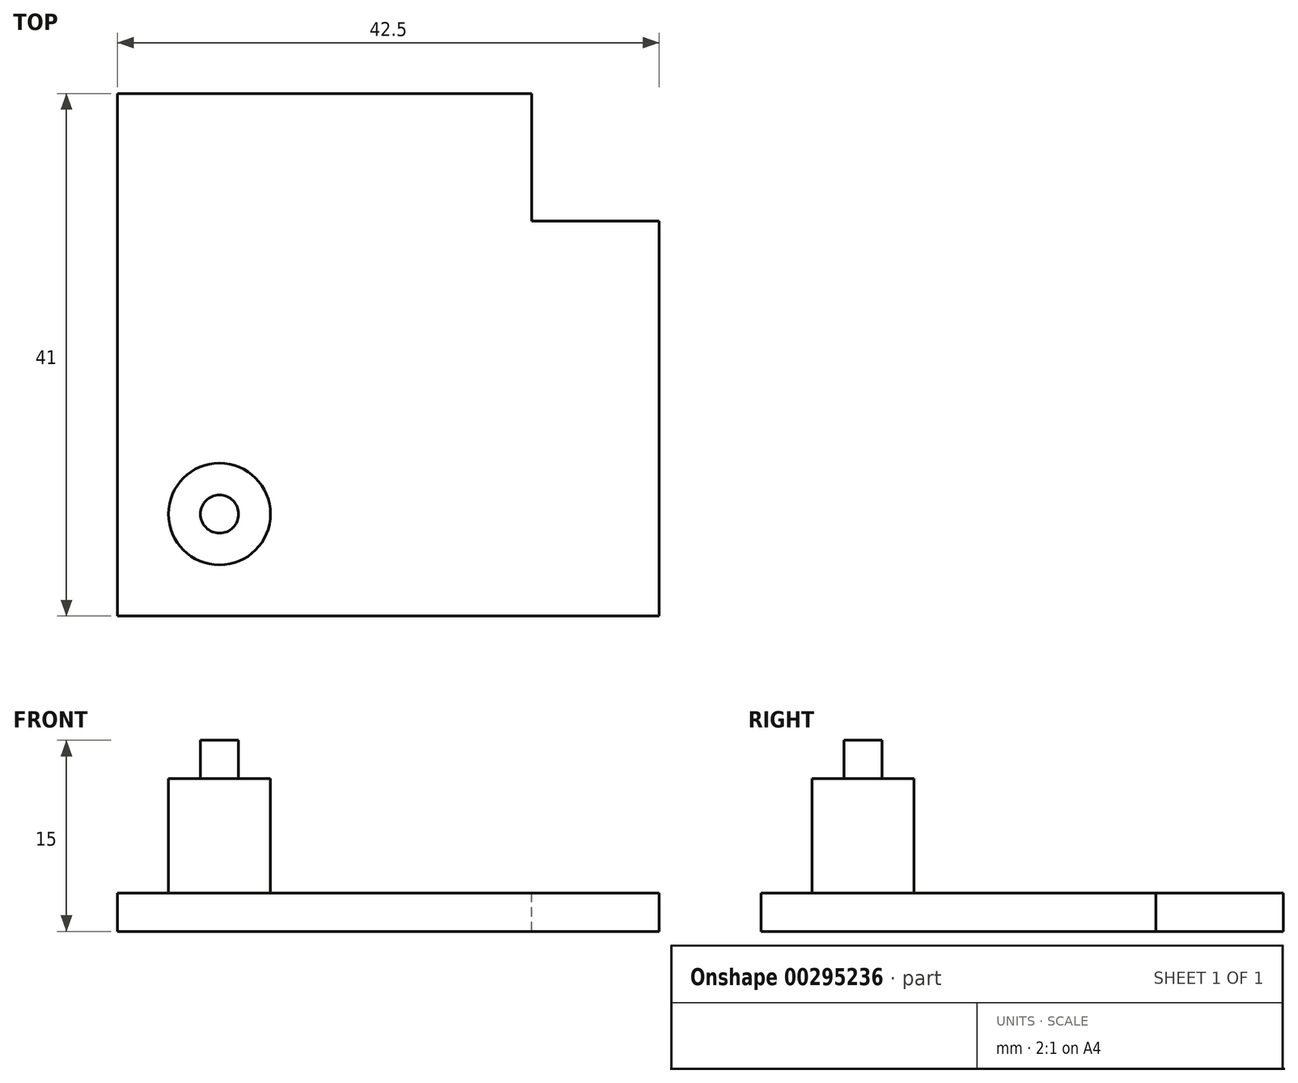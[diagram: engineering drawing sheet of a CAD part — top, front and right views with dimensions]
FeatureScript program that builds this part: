
annotation { "Feature Type Name" : "Feature", "Feature Type Description" : "" }
export const myFeature = defineFeature(function(context is Context, id is Id, definition is map)
    precondition{}
    {
        {
            var Q0;
            Q0=qCreatedBy(makeId("Top.planeOp"),FACE);
            var sketch = newSketch(context, id + "F0", { "sketchPlane" : qUnion([Q0])});
            skLineSegment(sketch, "E0", {"start": v(0, 0) * mm, "end": v(42.5, 0) * mm});
            skLineSegment(sketch, "E1", {"start": v(42.5, 0) * mm, "end": v(42.5, 31) * mm});
            skLineSegment(sketch, "E2", {"start": v(42.5, 31) * mm, "end": v(32.5, 31) * mm});
            skLineSegment(sketch, "E3", {"start": v(32.5, 31) * mm, "end": v(32.5, 41) * mm});
            skLineSegment(sketch, "E4", {"start": v(32.5, 41) * mm, "end": v(0, 41) * mm});
            skLineSegment(sketch, "E5", {"start": v(0, 41) * mm, "end": v(0, 0) * mm});
            skCircle(sketch, "E6", {"center": v(8, 8) * mm, "radius": 4 * mm});
            skSolve(sketch);
        }
        {
            var Q0;
            Q0=makeQuery(id+"F0.imprint","IMPRINT",FACE,{"disambiguationData":[TD([[makeQuery(id+"F0.imprint","IMPRINT",EDGE,{"derivedFrom":sQuery(id+"F0.wireOp",EDGE,"E6")}),1.0]])]});
            var Q1;
            Q1=makeQuery(id+"F0.imprint","IMPRINT",FACE,{"disambiguationData":[TD([[makeQuery(id+"F0.imprint","IMPRINT",EDGE,{"derivedFrom":sQuery(id+"F0.wireOp",EDGE,"E0")}),1.0]])]});
            extrude(context, id + "F1", {"entities" : qUnion([Q0, Q1]), "oppositeDirection" : true, "depth" : 3 * mm});
        }
        {
            var Q0;
            Q0=makeQuery(id+"F0.imprint","IMPRINT",FACE,{"disambiguationData":[TD([[makeQuery(id+"F0.imprint","IMPRINT",EDGE,{"derivedFrom":sQuery(id+"F0.wireOp",EDGE,"E6")}),1.0]])]});
            extrude(context, id + "F2", {"entities" : qUnion([Q0]), "operationType" : NewBodyOperationType.ADD, "depth" : 9 * mm});
        }
        {
            var Q0;
            Q0=makeQuery(id+"F2.opExtrude","CAP_FACE",FACE,{"disambiguationData":[OSD([sQuery(id+"F0.wireOp",EDGE,"E6")])],"isStart":false});
            var sketch = newSketch(context, id + "F3", { "sketchPlane" : qUnion([Q0])});
            skCircle(sketch, "E7", {"center": v(8, 8) * mm, "radius": 1.5 * mm});
            skSolve(sketch);
        }
        {
            var Q0;
            Q0=makeQuery(id+"F3.imprint","IMPRINT",FACE,{"disambiguationData":[TD([[makeQuery(id+"F3.imprint","IMPRINT",EDGE,{"derivedFrom":sQuery(id+"F3.wireOp",EDGE,"E7")}),1.0]])]});
            extrude(context, id + "F4", {"entities" : qUnion([Q0]), "operationType" : NewBodyOperationType.ADD, "depth" : 3 * mm});
        }
    });
